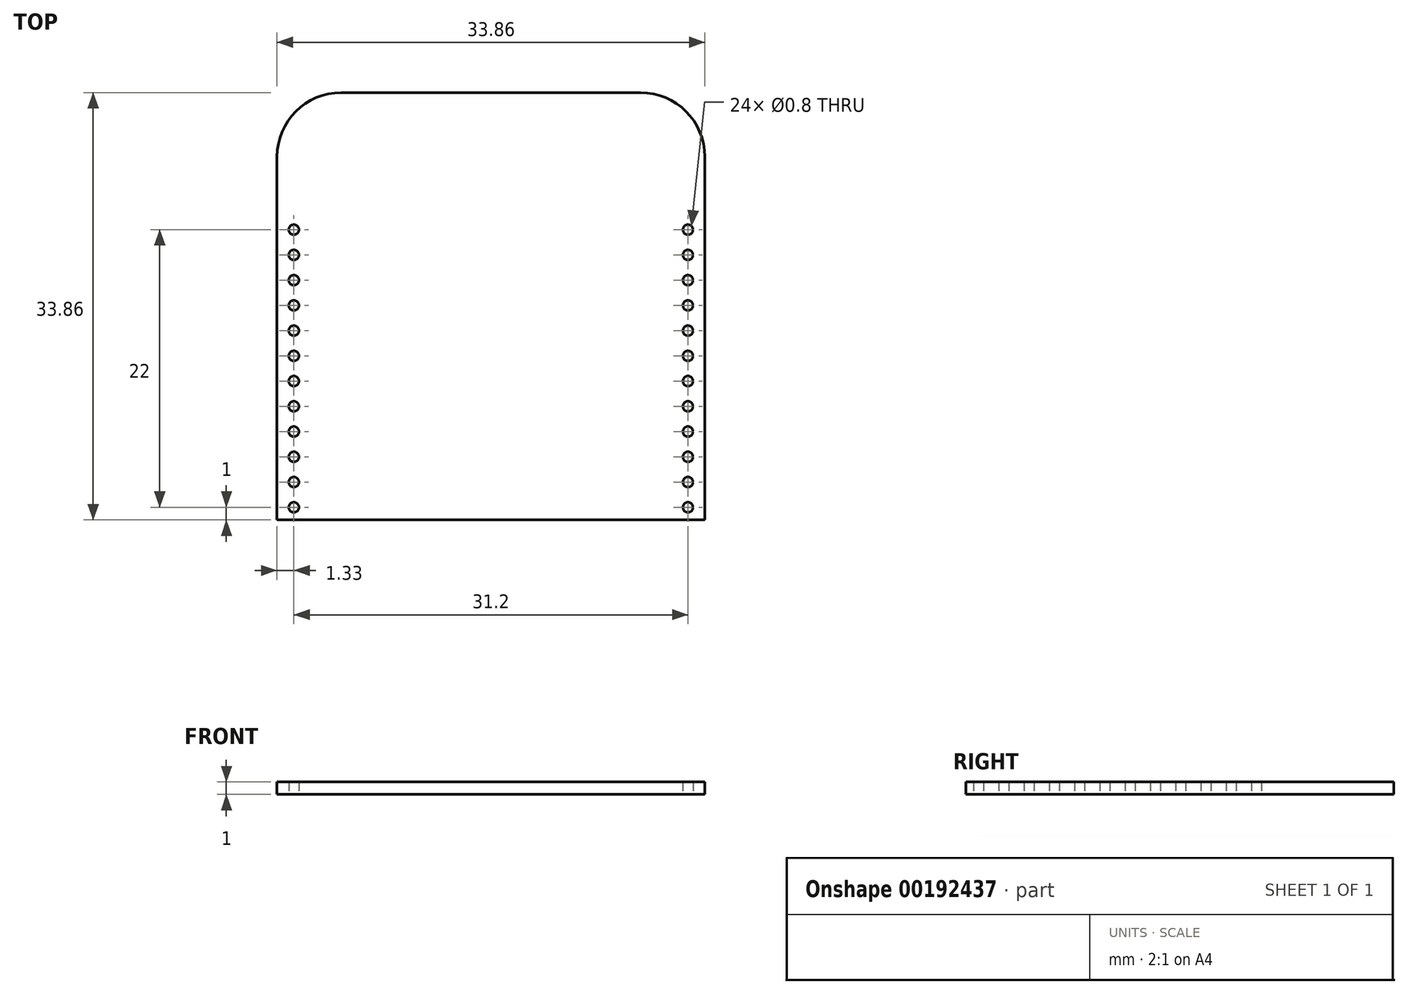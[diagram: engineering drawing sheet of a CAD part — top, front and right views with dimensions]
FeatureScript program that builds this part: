
annotation { "Feature Type Name" : "Feature", "Feature Type Description" : "" }
export const myFeature = defineFeature(function(context is Context, id is Id, definition is map)
    precondition{}
    {
        {
            var Q0;
            Q0=qCreatedBy(makeId("Top.planeOp"),FACE);
            var sketch = newSketch(context, id + "F0", { "sketchPlane" : qUnion([Q0])});
            skLineSegment(sketch, "E0.bottom", {"start": v(16.93, -16.93) * mm, "end": v(-16.93, -16.93) * mm});
            skLineSegment(sketch, "E0.top", {"start": v(11.85, 16.93) * mm, "end": v(-11.85, 16.93) * mm});
            skLineSegment(sketch, "E0.left", {"start": v(16.93, -16.93) * mm, "end": v(16.93, 11.85) * mm});
            skLineSegment(sketch, "E0.right", {"start": v(-16.93, -16.93) * mm, "end": v(-16.93, 11.85) * mm});
            skPoint(sketch, "E0.middle", {"position": v(0, 0) * mm});
            skPoint(sketch, "E1.visualSharp", {"position": v(-16.93, 16.93) * mm});
            skArc(sketch, "E1.filletArc", {"start": v(-11.85, 16.93) * mm, "mid": v(-15.44, 15.44) * mm, "end": v(-16.93, 11.85) * mm});
            skPoint(sketch, "E2.visualSharp", {"position": v(16.93, 16.93) * mm});
            skArc(sketch, "E2.filletArc", {"start": v(16.93, 11.85) * mm, "mid": v(15.44, 15.44) * mm, "end": v(11.85, 16.93) * mm});
            skCircle(sketch, "E3", {"center": v(15.6, -15.93) * mm, "radius": 0.4 * mm});
            skCircle(sketch, "E4.MirrorC", {"center": v(-15.6, -15.93) * mm, "radius": 0.4 * mm});
            skCircle(sketch, "E5.1.0.0", {"center": v(15.6, -13.93) * mm, "radius": 0.4 * mm});
            skCircle(sketch, "E5.1.0.1", {"center": v(-15.6, -13.93) * mm, "radius": 0.4 * mm});
            skCircle(sketch, "E5.2.0.0", {"center": v(15.6, -11.93) * mm, "radius": 0.4 * mm});
            skCircle(sketch, "E5.2.0.1", {"center": v(-15.6, -11.93) * mm, "radius": 0.4 * mm});
            skLineSegment(sketch, "E5.direction1", {"start": v(15.6, -15.93) * mm, "end": v(15.6, -13.93) * mm, "construction": true});
            skCircle(sketch, "E6.0.3.0", {"center": v(15.6, -9.93) * mm, "radius": 0.4 * mm});
            skCircle(sketch, "E6.2.3.0", {"center": v(-15.6, -9.93) * mm, "radius": 0.4 * mm});
            skCircle(sketch, "E6.0.4.0", {"center": v(15.6, -7.93) * mm, "radius": 0.4 * mm});
            skCircle(sketch, "E6.2.4.0", {"center": v(-15.6, -7.93) * mm, "radius": 0.4 * mm});
            skCircle(sketch, "E6.0.5.0", {"center": v(15.6, -5.93) * mm, "radius": 0.4 * mm});
            skCircle(sketch, "E6.2.5.0", {"center": v(-15.6, -5.93) * mm, "radius": 0.4 * mm});
            skCircle(sketch, "E6.0.6.0", {"center": v(15.6, -3.93) * mm, "radius": 0.4 * mm});
            skCircle(sketch, "E6.2.6.0", {"center": v(-15.6, -3.93) * mm, "radius": 0.4 * mm});
            skCircle(sketch, "E6.0.7.0", {"center": v(15.6, -1.93) * mm, "radius": 0.4 * mm});
            skCircle(sketch, "E6.2.7.0", {"center": v(-15.6, -1.93) * mm, "radius": 0.4 * mm});
            skCircle(sketch, "E6.0.8.0", {"center": v(15.6, 0.07) * mm, "radius": 0.4 * mm});
            skCircle(sketch, "E6.2.8.0", {"center": v(-15.6, 0.07) * mm, "radius": 0.4 * mm});
            skCircle(sketch, "E6.0.9.0", {"center": v(15.6, 2.07) * mm, "radius": 0.4 * mm});
            skCircle(sketch, "E6.2.9.0", {"center": v(-15.6, 2.07) * mm, "radius": 0.4 * mm});
            skCircle(sketch, "E7.0.10.0", {"center": v(15.6, 4.07) * mm, "radius": 0.4 * mm});
            skCircle(sketch, "E7.2.10.0", {"center": v(-15.6, 4.07) * mm, "radius": 0.4 * mm});
            skCircle(sketch, "E7.0.11.0", {"center": v(15.6, 6.07) * mm, "radius": 0.4 * mm});
            skCircle(sketch, "E7.2.11.0", {"center": v(-15.6, 6.07) * mm, "radius": 0.4 * mm});
            skSolve(sketch);
        }
        {
            var Q0;
            Q0 = qSketchRegion(id + "F0", true);
            extrude(context, id + "F1", {"entities" : qUnion([Q0]), "depth" : 1 * mm});
        }
    });
